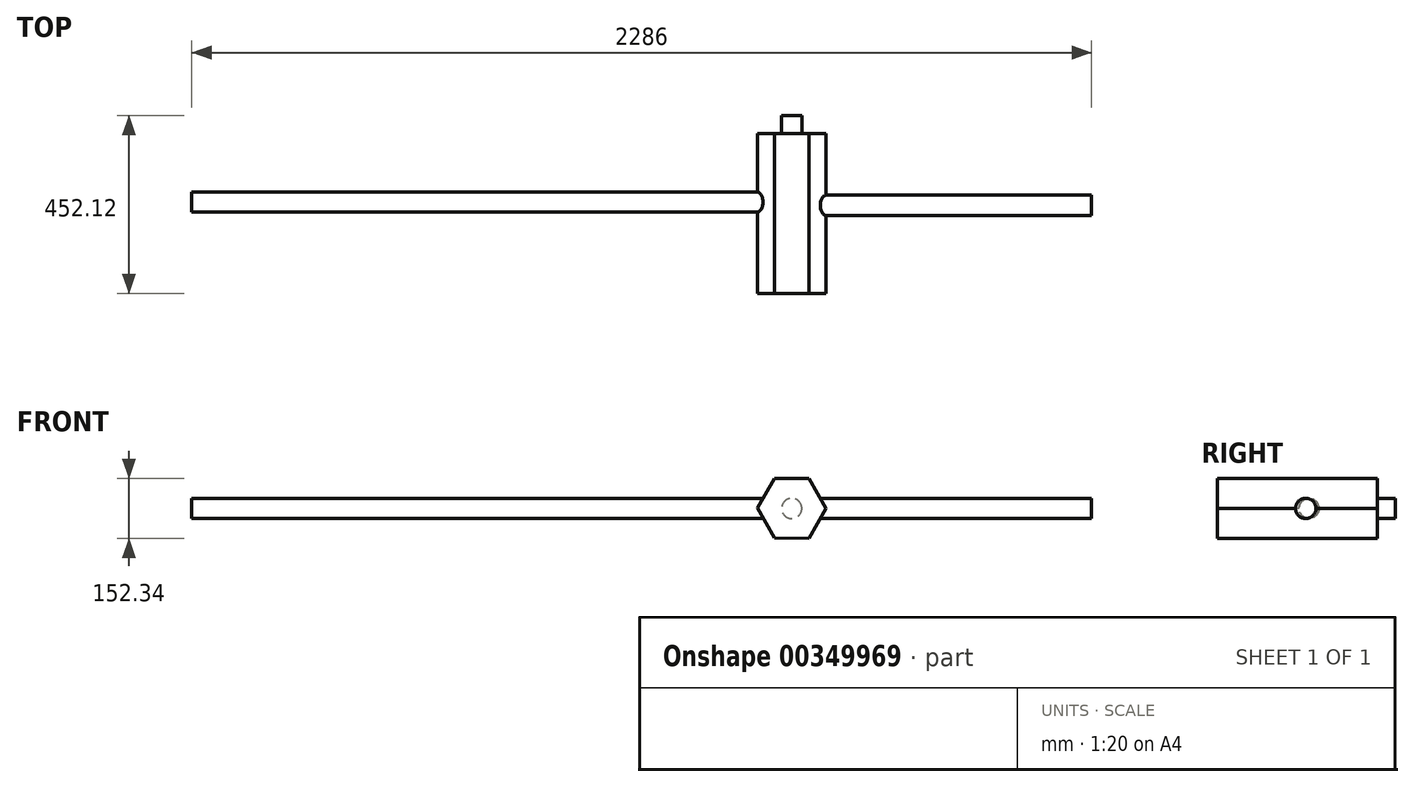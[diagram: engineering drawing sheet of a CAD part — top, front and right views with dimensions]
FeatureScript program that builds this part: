
annotation { "Feature Type Name" : "Feature", "Feature Type Description" : "" }
export const myFeature = defineFeature(function(context is Context, id is Id, definition is map)
    precondition{}
    {
        {
            var Q0;
            Q0=qCreatedBy(makeId("Front.planeOp"),FACE);
            var sketch = newSketch(context, id + "F0", { "sketchPlane" : qUnion([Q0])});
            skCircle(sketch, "E0.cCircle", {"center": v(0, 0) * mm, "radius": 75.88 * mm, "construction": true});
            skLineSegment(sketch, "E0.0", {"start": v(87.61, -0.6) * mm, "end": v(43.3, -76.17) * mm});
            skLineSegment(sketch, "E0.1", {"start": v(43.3, -76.17) * mm, "end": v(-44.32, -75.58) * mm});
            skLineSegment(sketch, "E0.2", {"start": v(-44.32, -75.58) * mm, "end": v(-87.61, 0.6) * mm});
            skLineSegment(sketch, "E0.3", {"start": v(-87.61, 0.6) * mm, "end": v(-43.3, 76.17) * mm});
            skLineSegment(sketch, "E0.4", {"start": v(-43.3, 76.17) * mm, "end": v(44.32, 75.58) * mm});
            skLineSegment(sketch, "E0.5", {"start": v(44.32, 75.58) * mm, "end": v(87.61, -0.6) * mm});
            skPoint(sketch, "E0.0.midPoint", {"position": v(65.45, -38.38) * mm});
            skSolve(sketch);
        }
        {
            var Q0;
            Q0 = qSketchRegion(id + "F0", true);
            extrude(context, id + "F1", {"entities" : qUnion([Q0]), "depth" : 406.4 * mm});
        }
        {
            var Q0;
            Q0=qCreatedBy(makeId("Right.planeOp"),FACE);
            var sketch = newSketch(context, id + "F2", { "sketchPlane" : qUnion([Q0])});
            skCircle(sketch, "E1", {"center": v(-182.55, 0) * mm, "radius": 25.88 * mm});
            skSolve(sketch);
        }
        {
            var Q0;
            Q0 = qSketchRegion(id + "F2", true);
            extrude(context, id + "F3", {"entities" : qUnion([Q0]), "operationType" : NewBodyOperationType.ADD, "depth" : 762 * mm});
        }
        {
            var Q0;
            Q0=qCreatedBy(makeId("Right.planeOp"),FACE);
            var sketch = newSketch(context, id + "F4", { "sketchPlane" : qUnion([Q0])});
            skCircle(sketch, "E2", {"center": v(-174.27, 0) * mm, "radius": 25.4 * mm});
            skSolve(sketch);
        }
        {
            var Q0;
            Q0 = qSketchRegion(id + "F4", true);
            extrude(context, id + "F5", {"entities" : qUnion([Q0]), "operationType" : NewBodyOperationType.ADD, "oppositeDirection" : true, "depth" : 1524 * mm});
        }
        {
            var Q0;
            Q0=qCreatedBy(makeId("Front.planeOp"),FACE);
            var sketch = newSketch(context, id + "F6", { "sketchPlane" : qUnion([Q0])});
            skCircle(sketch, "E3", {"center": v(0, 0) * mm, "radius": 25.68 * mm});
            skSolve(sketch);
        }
        {
            var Q0;
            Q0 = qSketchRegion(id + "F6", true);
            extrude(context, id + "F7", {"entities" : qUnion([Q0]), "operationType" : NewBodyOperationType.ADD, "oppositeDirection" : true, "depth" : 45.72 * mm});
        }
    });
